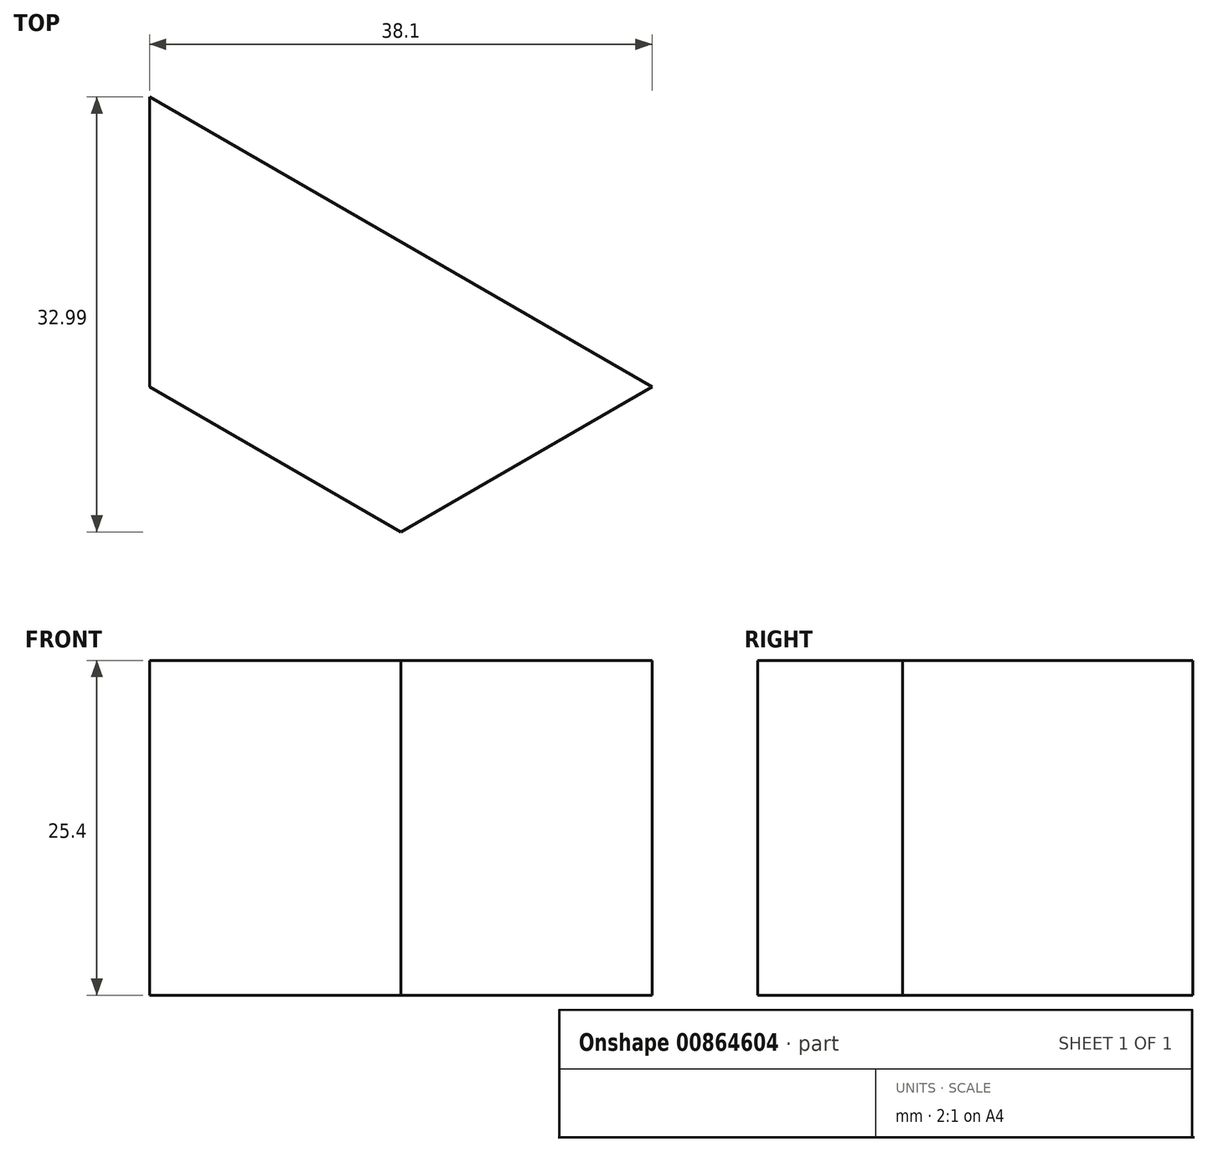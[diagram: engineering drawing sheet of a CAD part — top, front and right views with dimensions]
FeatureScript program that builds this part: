
annotation { "Feature Type Name" : "Feature", "Feature Type Description" : "" }
export const myFeature = defineFeature(function(context is Context, id is Id, definition is map)
    precondition{}
    {
        {
            var Q0;
            Q0=qCreatedBy(makeId("Top.planeOp"),FACE);
            var sketch = newSketch(context, id + "F0", { "sketchPlane" : qUnion([Q0])});
            skCircle(sketch, "E0.cCircle", {"center": v(0, 0) * mm, "radius": 19.05 * mm, "construction": true});
            skLineSegment(sketch, "E0.0", {"start": v(19.05, 11) * mm, "end": v(19.05, -11) * mm, "construction": true});
            skLineSegment(sketch, "E0.1", {"start": v(19.05, -11) * mm, "end": v(0, -22) * mm, "construction": true});
            skLineSegment(sketch, "E0.2", {"start": v(0, -22) * mm, "end": v(-19.05, -11) * mm, "construction": true});
            skLineSegment(sketch, "E0.3", {"start": v(-19.05, -11) * mm, "end": v(-19.05, 11) * mm, "construction": true});
            skLineSegment(sketch, "E0.4", {"start": v(-19.05, 11) * mm, "end": v(0, 22) * mm, "construction": true});
            skLineSegment(sketch, "E0.5", {"start": v(0, 22) * mm, "end": v(19.05, 11) * mm});
            skPoint(sketch, "E0.0.midPoint", {"position": v(19.05, 0) * mm});
            skLineSegment(sketch, "E1", {"start": v(0, 22) * mm, "end": v(0, 44) * mm});
            skLineSegment(sketch, "E2", {"start": v(0, 44) * mm, "end": v(38.1, 22) * mm});
            skLineSegment(sketch, "E3", {"start": v(38.1, 22) * mm, "end": v(19.05, 11) * mm});
            skLineSegment(sketch, "E4", {"start": v(19.05, 11) * mm, "end": v(-19.05, -11) * mm, "construction": true});
            skSolve(sketch);
        }
        {
            var Q0;
            Q0 = qSketchRegion(id + "F0", true);
            extrude(context, id + "F1", {"entities" : qUnion([Q0]), "depth" : 25.4 * mm, "offsetDistance" : 25.4 * mm});
        }
    });
